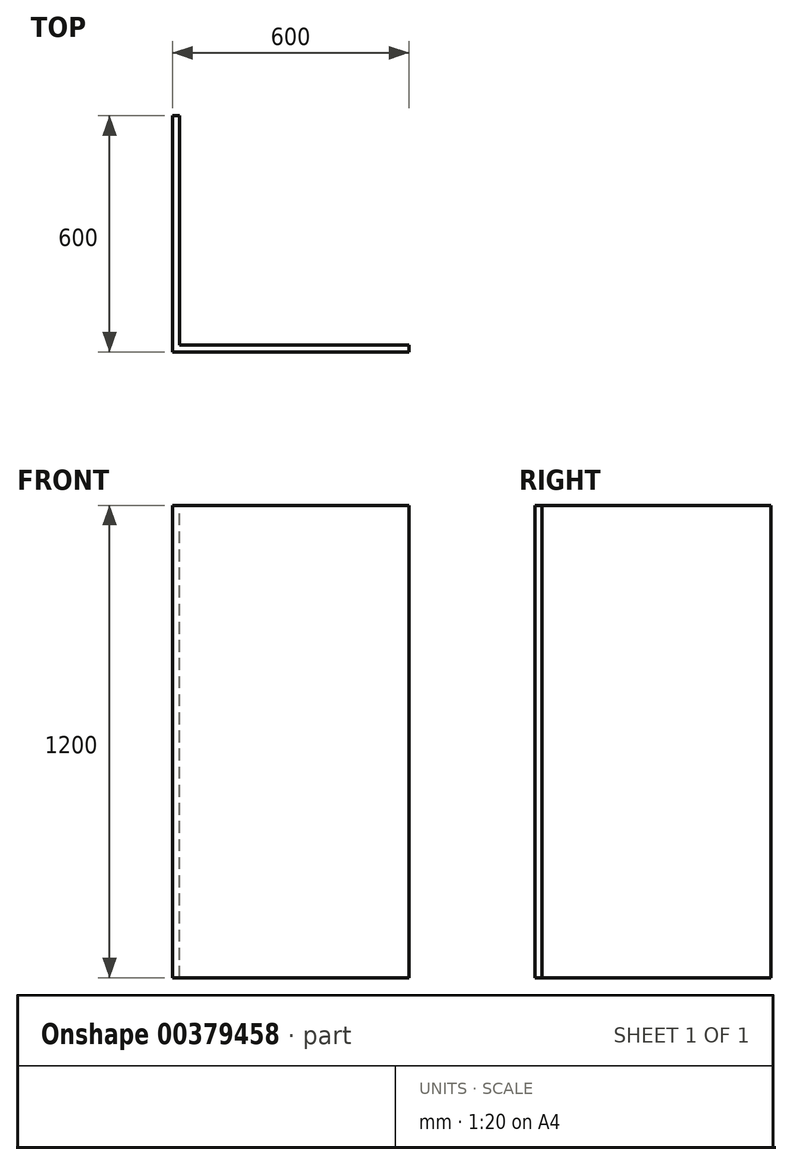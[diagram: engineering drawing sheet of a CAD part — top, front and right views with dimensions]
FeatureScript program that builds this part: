
annotation { "Feature Type Name" : "Feature", "Feature Type Description" : "" }
export const myFeature = defineFeature(function(context is Context, id is Id, definition is map)
    precondition{}
    {
        {
            var Q0;
            Q0=qCreatedBy(makeId("Front.planeOp"),FACE);
            var sketch = newSketch(context, id + "F0", { "sketchPlane" : qUnion([Q0])});
            skLineSegment(sketch, "E0.bottom", {"start": v(0, 0) * mm, "end": v(600, 0) * mm});
            skLineSegment(sketch, "E0.top", {"start": v(0, 1200) * mm, "end": v(600, 1200) * mm});
            skLineSegment(sketch, "E0.left", {"start": v(0, 0) * mm, "end": v(0, 1200) * mm});
            skLineSegment(sketch, "E0.right", {"start": v(600, 0) * mm, "end": v(600, 1200) * mm});
            skSolve(sketch);
        }
        {
            var Q0;
            Q0 = qSketchRegion(id + "F0", true);
            extrude(context, id + "F1", {"entities" : qUnion([Q0]), "oppositeDirection" : true, "depth" : 18 * mm});
        }
        {
            var Q0;
            Q0=makeQuery(id+"F1.opExtrude","SWEPT_FACE",FACE,{"disambiguationData":[OSD([sQuery(id+"F0.wireOp",EDGE,"E0.left")])]});
            var sketch = newSketch(context, id + "F2", { "sketchPlane" : qUnion([Q0])});
            skLineSegment(sketch, "E1.bottom", {"start": v(-18, 0) * mm, "end": v(-600, 0) * mm});
            skLineSegment(sketch, "E1.top", {"start": v(-18, 1200) * mm, "end": v(-600, 1200) * mm});
            skLineSegment(sketch, "E1.left", {"start": v(-18, 0) * mm, "end": v(-18, 1200) * mm});
            skLineSegment(sketch, "E1.right", {"start": v(-600, 0) * mm, "end": v(-600, 1200) * mm});
            skSolve(sketch);
        }
        {
            var Q0;
            Q0 = qSketchRegion(id + "F2", true);
            extrude(context, id + "F3", {"entities" : qUnion([Q0]), "operationType" : NewBodyOperationType.ADD, "oppositeDirection" : true, "depth" : 18 * mm});
        }
    });
